# Revit family: 2070093
name_source: partatom
category: Lighting Fixtures
revit_build: Autodesk Revit 2018 (Build: 20170223_1515(x64)
units: mm (PartAtom-declared; Revit-internal decimal feet)

## family parameters
Cut with Voids When Loaded = No
Host = Face
Light Source = No
OmniClass Number = 23.80.70.11.17
OmniClass Title = Specialized Lighting by Location or Use
Part Type = Normal
Room Calculation Point = No
Round Connector Dimension = Use Diameter
Shared = No

## types (1)
- 2070093 EXPOSPOT 90 MONO HO RA90 4000K MB WHITE
    Apparent Load = 35 VA
    Assembly Code = D5020200
    Average Life = 50 000h
    Beam Angle = 47°
    Body Material = Aluminum_Sylvania_Expospot_White
    Body Secondary Material = Plastic_Sylvania_Expospot_Black
    Body Void Radius = 58 mm
    CRI = 80Ra
    Colour Variation Initial = 3SDCM
    Control Gear Mounting = Remote
    Control Gear Required = No
    Control Gear Type = Electronic
    Default Elevation = 0 mm  [stored 0 ft]
    Description = Specifically designed for Retail and Display applications. I.e. Supermarkets, Fashion Retail, Department stores. Build around a 90mm reflector and lens combination.
    Diffuser Material = Acrylic_Sylvania_Expospot_3000K
    Dimmable = N
    Drive Current = 700mA
    Electrical Protection = Class II
    Glow Wire Test = 850 °C
    Head Diameter = 100 mm  [stored 0.328084 ft]
    Head Radius = 50 mm  [stored 0.164042 ft]
    Height = 104 mm
    IK Rating = IK02
    IP Rating = IP20
    Initial Color = 3000 K
    Initial Intensity = 3126 lm
    Inrush Current = 19 A
    Inrush Duration = 250µs
    LOR = 100%
    Lamp = LED
    Lamp Power Factor = 0.92
    Light Loss Factor = 1
    Manufacturer = Feilo Sylvania
    Max. Luminaires per 10A B Breaker = 13
    Max. Luminaires per 10A C Breaker = 21
    Max. Luminaires per 13A B Breaker = 17
    Max. Luminaires per 13A C Breaker = 28
    Max. Luminaires per 16A B Breaker = 21
    Max. Luminaires per 16A C Breaker = 35
    Max. Luminaires per 20A B Breaker = 27
    Max. Luminaires per 20A C Breaker = 45
    Model = EXPOSPOT 90 MONO HO RA90 4000K MB WHITE
    Mounting Width Inner = 55 mm  [stored 0.180446 ft]
    Mounting Width Outer = 63 mm  [stored 0.206693 ft]
    Nominal Frequency = 50/60Hz
    Photobiological Risk Group = RG1
    Photometric Web File = IES_Expospot_90_Cardan_Square : 0060385
    Product Code = 0060301
    Product Family = EXPOSPOT 90 CARDAN
    Product Page URL = http://www.sylvania-lighting.com
    Reflector Material = Aluminum_Sylvania_Expospot_Polished
    Total Power Consumption = 28 W
    URL = 0.95
    Voltage = 240 V
    Voltage Comments = 220-240V~
    Weight = 1 kg
    Width = 163 mm  [stored 0.534777 ft]

note: [stored X ft] marks values corroborated as IEEE doubles in the binary element streams (Revit-internal decimal feet)

## geometry (parser evidence)
native form markers: Sweep x8
no freeform markers — native parametric forms only
